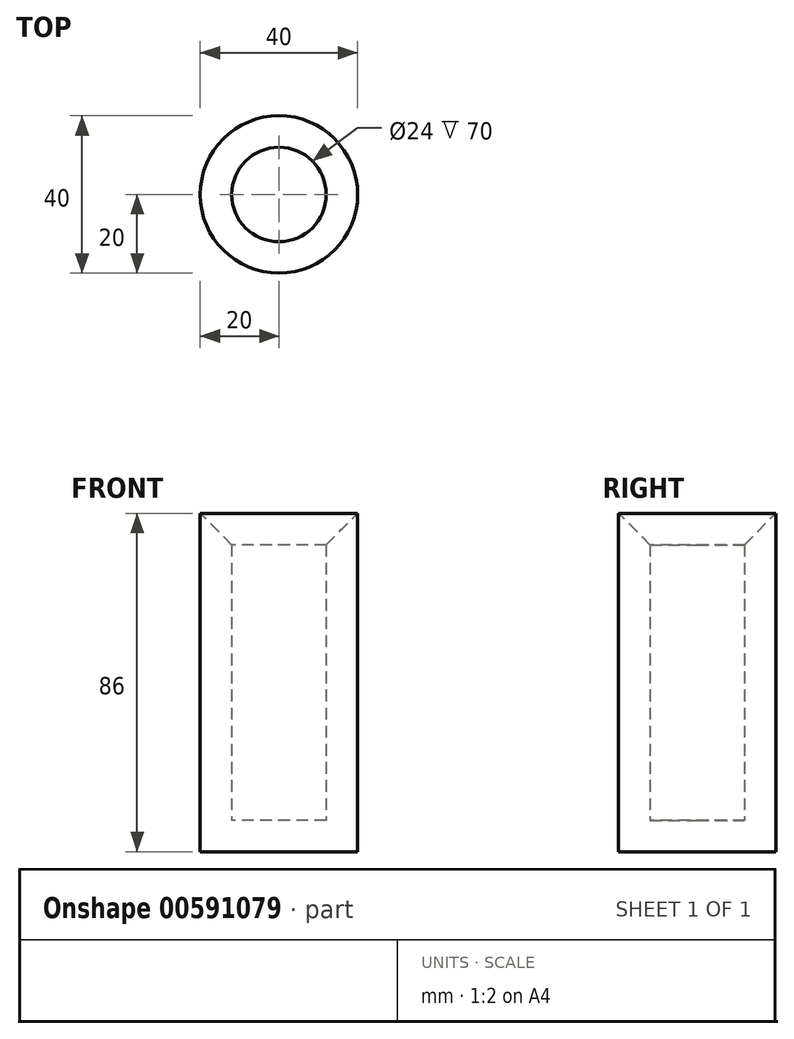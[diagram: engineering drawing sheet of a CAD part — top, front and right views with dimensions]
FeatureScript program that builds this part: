
annotation { "Feature Type Name" : "Feature", "Feature Type Description" : "" }
export const myFeature = defineFeature(function(context is Context, id is Id, definition is map)
    precondition{}
    {
        {
            var Q0;
            Q0=qCreatedBy(makeId("Top.planeOp"),FACE);
            var sketch = newSketch(context, id + "F0", { "sketchPlane" : qUnion([Q0])});
            skCircle(sketch, "E0", {"center": v(0, 0) * mm, "radius": 20 * mm});
            skSolve(sketch);
        }
        {
            var Q0;
            Q0=makeQuery(id+"F0.imprint","IMPRINT",FACE,{"disambiguationData":[TD([[makeQuery(id+"F0.imprint","IMPRINT",EDGE,{"derivedFrom":sQuery(id+"F0.wireOp",EDGE,"E0")}),1.0]])]});
            extrude(context, id + "F1", {"entities" : qUnion([Q0]), "depth" : 86 * mm, "offsetDistance" : 25 * mm});
        }
        {
            var Q0;
            Q0=makeQuery(id+"F1.opExtrude","CAP_FACE",FACE,{"disambiguationData":[OSD([sQuery(id+"F0.wireOp",EDGE,"E0")])],"isStart":false});
            shell(context, id + "F2", {"entities" : qUnion([Q0]), "thickness" : 8 * mm});
        }
        {
            var Q0;
            {var subQ0=sQuery(id+"F0.wireOp",EDGE,"E0");Q0=makeQuery(id+"F2.opShell","OFFSET_EDGE",EDGE,{"disambiguationData":[OSD([subQ0]),TDD([makeQuery(id+"F1.opExtrude","CAP_EDGE",EDGE,{"disambiguationData":[OSD([subQ0])],"isStart":false})])]});}
            chamfer(context, id + "F3", {"entities" : qUnion([Q0]), "width" : 8 * mm, "tangentPropagation" : true});
        }
    });
